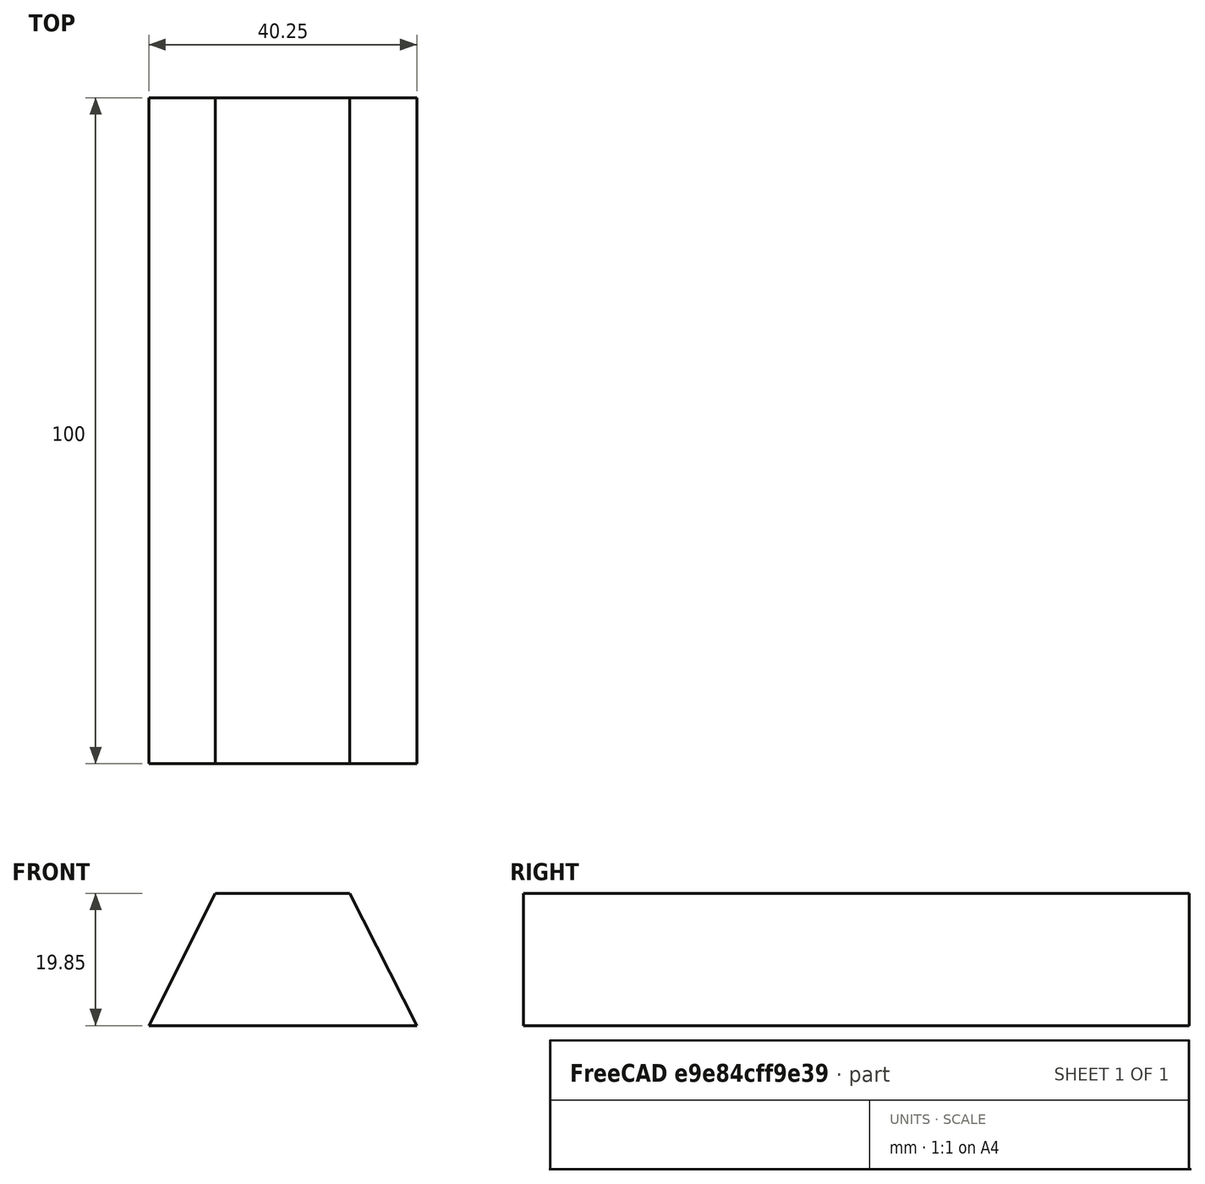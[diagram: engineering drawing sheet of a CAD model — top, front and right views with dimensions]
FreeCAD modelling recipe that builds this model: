
FCSTD DOCUMENT  (FreeCAD 0.21R33694 (Git))
Label: OJT1_T16R01.orr
License: All rights reserved
LicenseURL: http://en.wikipedia.org/wiki/All_rights_reserved
objects: Sketcher::SketchObject×1, PartDesign::Pad×1, PartDesign::Body×1
note: 4 computed .brp shape members not serialized (recipe doc carries the construction recipe); baked Part::Feature solids carry a one-line shape summary decoded from their .brp

FEATURE [Sketcher::SketchObject] Sketch
  FullyConstrained = false
  MapMode = 5
  Placement = pos=(0,0,0) rot=(1,0,0;1.5708rad)
  Support = -> [XZ_Plane]
  sketch-geometry (4):
    g0: LineSegment StartX=-10.1827 StartY=9.91873 StartZ=0 EndX=9.99581 EndY=9.91873 EndZ=0
    g1: LineSegment StartX=9.99581 StartY=9.91873 StartZ=0 EndX=20.0851 EndY=-9.92719 EndZ=0
    g2: LineSegment StartX=20.0851 StartY=-9.92719 StartZ=0 EndX=-20.1611 EndY=-9.92719 EndZ=0
    g3: LineSegment StartX=-20.1611 StartY=-9.92719 StartZ=0 EndX=-10.1827 EndY=9.91873 EndZ=0
  constraints (6):
    c: Horizontal(g0)
    c: Coincident(g0,g1)
    c: Coincident(g1,g2)
    c: Horizontal(g2)
    c: Coincident(g2,g3)
    c: Coincident(g3,g0)
FEATURE [PartDesign::Pad] Pad
  Direction = (0,-1,2e-16)
  Length = 100
  Length2 = 10
  Placement = pos=(0,0,0) rot=(1,0,0;1.5708rad)
  Profile = -> Sketch
  ReferenceAxis = -> Sketch [N_Axis]
  Refine = true
  Type = 0
FEATURE [PartDesign::Body] Body
  Group = -> [Sketch,Pad]
  Origin = -> Origin
  Tip = -> Pad
